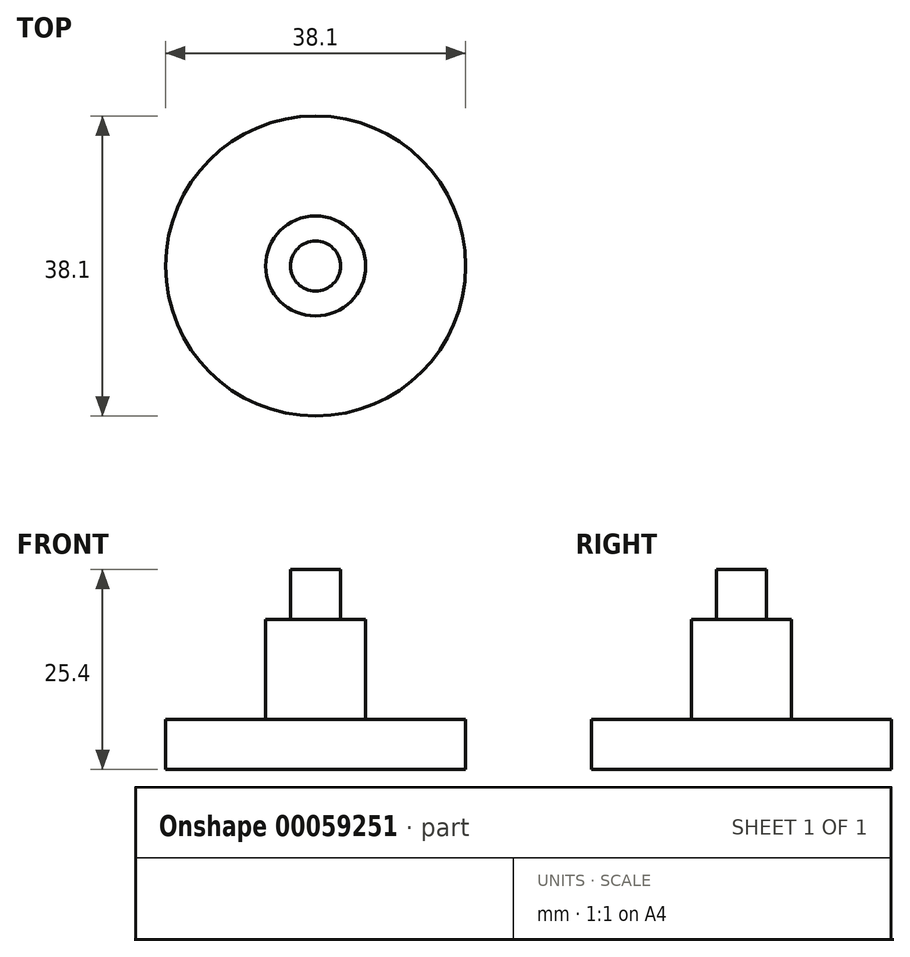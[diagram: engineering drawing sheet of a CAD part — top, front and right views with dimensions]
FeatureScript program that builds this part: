
annotation { "Feature Type Name" : "Feature", "Feature Type Description" : "" }
export const myFeature = defineFeature(function(context is Context, id is Id, definition is map)
    precondition{}
    {
        {
            var Q0;
            Q0=qCreatedBy(makeId("Front.planeOp"),FACE);
            var sketch = newSketch(context, id + "F0", { "sketchPlane" : qUnion([Q0])});
            skLineSegment(sketch, "E0.bottom", {"start": v(3.75, -5.21) * mm, "end": v(6.92, -5.21) * mm});
            skLineSegment(sketch, "E0.right", {"start": v(6.92, -5.21) * mm, "end": v(6.92, -17.91) * mm});
            skLineSegment(sketch, "E1", {"start": v(0.57, 1.14) * mm, "end": v(3.75, 1.14) * mm});
            skLineSegment(sketch, "E2", {"start": v(3.75, 1.14) * mm, "end": v(3.75, -5.21) * mm});
            skLineSegment(sketch, "E3.bottom", {"start": v(6.92, -17.91) * mm, "end": v(19.62, -17.91) * mm});
            skLineSegment(sketch, "E3.top", {"start": v(0.57, -24.26) * mm, "end": v(19.62, -24.26) * mm});
            skLineSegment(sketch, "E3.right", {"start": v(19.62, -17.91) * mm, "end": v(19.62, -24.26) * mm});
            skLineSegment(sketch, "E4", {"start": v(0.57, 1.14) * mm, "end": v(0.57, -24.26) * mm});
            skSolve(sketch);
        }
        {
            var Q0;
            Q0 = qSketchRegion(id + "F0", true);
            var Q1;
            Q1=sQuery(id+"F0.wireOp",EDGE,"E4");
            revolve(context, id + "F1", {"entities" : qUnion([Q0]), "axis" : qUnion([Q1]), "revolveType" : RevolveType.FULL});
        }
    });
